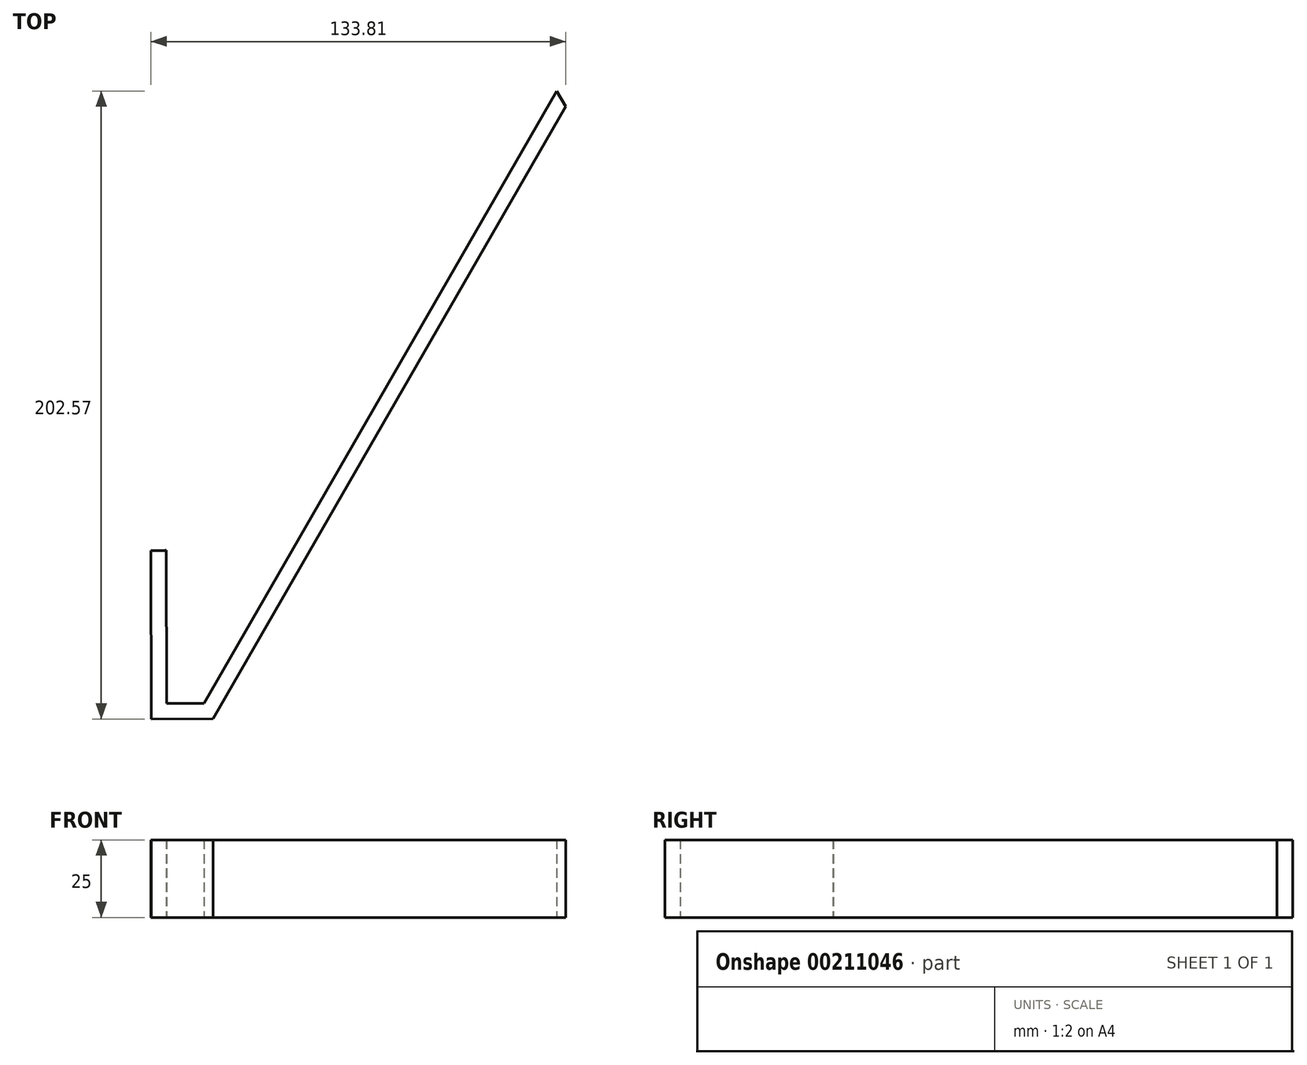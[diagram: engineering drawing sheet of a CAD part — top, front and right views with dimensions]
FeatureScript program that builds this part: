
annotation { "Feature Type Name" : "Feature", "Feature Type Description" : "" }
export const myFeature = defineFeature(function(context is Context, id is Id, definition is map)
    precondition{}
    {
        {
            var Q0;
            Q0=qCreatedBy(makeId("Top.planeOp"),FACE);
            var sketch = newSketch(context, id + "F0", { "sketchPlane" : qUnion([Q0])});
            skCircle(sketch, "E0.cCircle", {"center": v(0, 0) * mm, "radius": 177.8 * mm, "construction": true});
            skLineSegment(sketch, "E0.0", {"start": v(153.87, 89.08) * mm, "end": v(0.21, -177.8) * mm});
            skLineSegment(sketch, "E0.1", {"start": v(0.21, -177.8) * mm, "end": v(-154.08, 88.72) * mm});
            skLineSegment(sketch, "E0.2", {"start": v(-154.08, 88.72) * mm, "end": v(153.87, 89.08) * mm});
            skArc(sketch, "E1", {"start": v(87.38, -16.4) * mm, "mid": v(-77.04, 44.36) * mm, "end": v(58.04, -67.34) * mm});
            skLineSegment(sketch, "E2", {"start": v(-134.04, 54.1) * mm, "end": v(-114.08, 88.77) * mm});
            skLineSegment(sketch, "E3", {"start": v(-19.83, -143.18) * mm, "end": v(20.17, -143.14) * mm});
            skLineSegment(sketch, "E4", {"start": v(113.87, 89.03) * mm, "end": v(133.92, 54.42) * mm});
            skLineSegment(sketch, "E5", {"start": v(0.21, -177.8) * mm, "end": v(0, 0) * mm});
            skLineSegment(sketch, "E6", {"start": v(153.87, 89.08) * mm, "end": v(0, 0) * mm});
            skLineSegment(sketch, "E7", {"start": v(0, 0) * mm, "end": v(-154.08, 88.72) * mm});
            skArc(sketch, "E8.0", {"start": v(5.11, -93.76) * mm, "mid": v(29.4, -89.18) * mm, "end": v(51.67, -78.4) * mm});
            skLineSegment(sketch, "E9.0", {"start": v(5.16, -138.15) * mm, "end": v(5, 0) * mm});
            skLineSegment(sketch, "E9.1", {"start": v(149.54, 91.58) * mm, "end": v(17.28, -138.14) * mm});
            skLineSegment(sketch, "E10.0", {"start": v(-19.84, -138.18) * mm, "end": v(0.16, -138.16) * mm});
            skLineSegment(sketch, "E11.trimOffspring", {"start": v(5.16, -138.15) * mm, "end": v(17.28, -138.14) * mm});
            skArc(sketch, "E12.trimOffspring", {"start": v(61.96, -70.56) * mm, "mid": v(81.38, -46.85) * mm, "end": v(92.13, -18.16) * mm});
            skArc(sketch, "E13.trimOffspring", {"start": v(93.75, -5.32) * mm, "mid": v(-64.53, 68.21) * mm, "end": v(0.11, -93.9) * mm});
            skSolve(sketch);
        }
        {
            var Q0;
            {var subQ22=sQuery(id+"F0.wireOp",EDGE,"E11.trimOffspring");Q0=makeQuery(id+"F0.imprint","IMPRINT",FACE,{"disambiguationData":[TD([[makeQuery(id+"F0.imprint","IMPRINT",EDGE,{"derivedFrom":subQ22}),-1.0]])]});}
            extrude(context, id + "F1", {"entities" : qUnion([Q0]), "depth" : 25 * mm});
        }
    });
